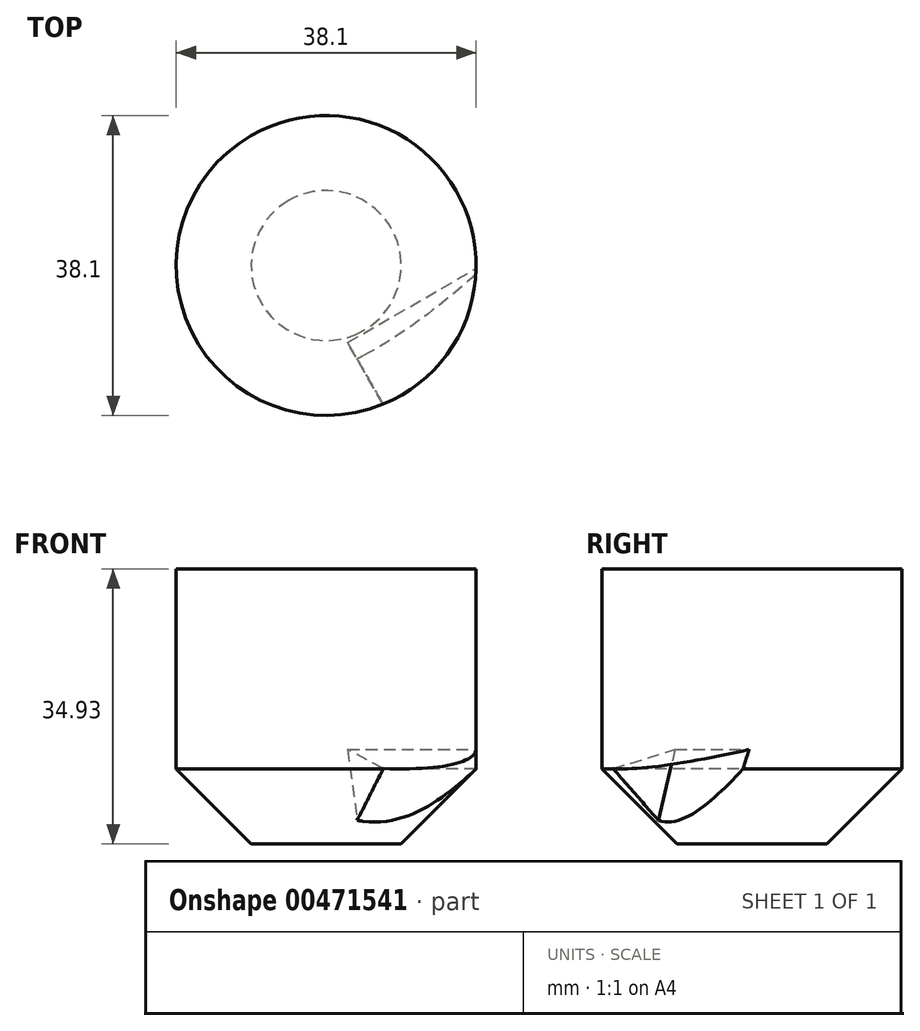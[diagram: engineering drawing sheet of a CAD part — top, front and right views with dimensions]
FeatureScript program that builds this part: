
annotation { "Feature Type Name" : "Feature", "Feature Type Description" : "" }
export const myFeature = defineFeature(function(context is Context, id is Id, definition is map)
    precondition{}
    {
        {
            var Q0;
            Q0=qCreatedBy(makeId("Top.planeOp"),FACE);
            var sketch = newSketch(context, id + "F0", { "sketchPlane" : qUnion([Q0])});
            skCircle(sketch, "E0", {"center": v(0, 0) * mm, "radius": 19.05 * mm});
            skSolve(sketch);
        }
        {
            var Q0;
            Q0=makeQuery(id+"F0.imprint","IMPRINT",FACE,{"disambiguationData":[TD([[makeQuery(id+"F0.imprint","IMPRINT",EDGE,{"derivedFrom":sQuery(id+"F0.wireOp",EDGE,"E0")}),1.0]])]});
            extrude(context, id + "F1", {"entities" : qUnion([Q0]), "depth" : 25.4 * mm});
        }
        {
            var Q0;
            Q0=makeQuery(id+"F1.opExtrude","CAP_FACE",FACE,{"disambiguationData":[OSD([sQuery(id+"F0.wireOp",EDGE,"E0")])],"isStart":true});
            extrude(context, id + "F2", {"entities" : qUnion([Q0]), "operationType" : NewBodyOperationType.ADD, "depth" : 9.52 * mm, "hasDraft" : true, "draftAngle" : 45 * degree, "draftPullDirection" : true});
        }
        {
            var Q0;
            Q0=qCreatedBy(makeId("Front.planeOp"),FACE);
            var sketch = newSketch(context, id + "F3", { "sketchPlane" : qUnion([Q0])});
            skLineSegment(sketch, "E1", {"start": v(-12.31, -6.74) * mm, "end": v(-19.05, 0) * mm});
            skLineSegment(sketch, "E2.0", {"start": v(-9.53, -9.53) * mm, "end": v(9.53, -9.53) * mm});
            skLineSegment(sketch, "E3", {"start": v(-19.05, 0) * mm, "end": v(-9.85, 2.47) * mm});
            skLineSegment(sketch, "E4", {"start": v(-9.85, 2.47) * mm, "end": v(-12.31, -6.74) * mm});
            skSolve(sketch);
        }
        {
            var Q0;
            Q0 = qSketchRegion(id + "F3", true);
            extrude(context, id + "F4", {"entities" : qUnion([Q0]), "operationType" : NewBodyOperationType.REMOVE, "oppositeDirection" : true, "depth" : 2.54 * mm});
        }
        {
            var Q0;
            Q0 = qSketchRegion(id + "F3", true);
            extrude(context, id + "F5", {"entities" : qUnion([Q0]), "operationType" : NewBodyOperationType.REMOVE, "depth" : 25.4 * mm});
        }
        {
            var Q0;
            Q0=makeQuery(id+"F1.opExtrude","SWEPT_BODY",BODY,{"disambiguationData":[OSD([sQuery(id+"F0.wireOp",EDGE,"E0")])]});
            var Q1;
            Q1=makeQuery(id+"F2.opExtrude","CAP_EDGE",EDGE,{"disambiguationData":[OSD([sQuery(id+"F0.wireOp",EDGE,"E0")])],"isStart":false});
            var Q2;
            Q2=makeQuery(id+"F2.opExtrude","CAP_EDGE",EDGE,{"disambiguationData":[OSD([sQuery(id+"F0.wireOp",EDGE,"E0")])],"isStart":false});
            transform(context, id + "F6", {"entities" : qUnion([Q0]), "transformType" : TransformType.ROTATION, "transformAxis" : qUnion([Q2]), "angle" : 120 * degree, "makeCopy" : false});
        }
    });
